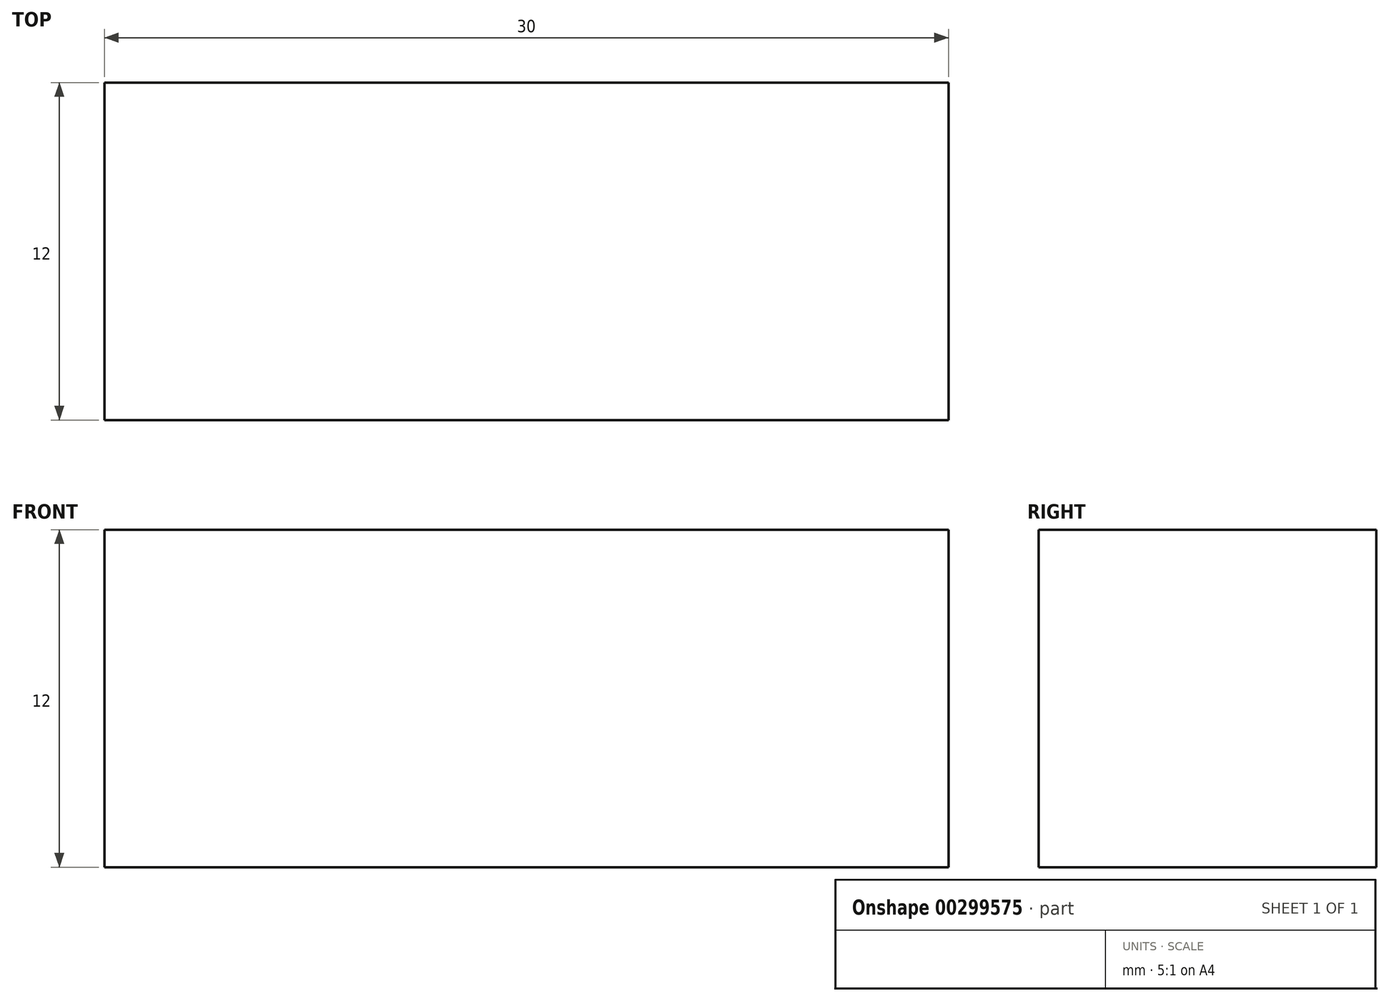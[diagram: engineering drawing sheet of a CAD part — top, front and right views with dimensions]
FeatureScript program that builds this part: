
annotation { "Feature Type Name" : "Feature", "Feature Type Description" : "" }
export const myFeature = defineFeature(function(context is Context, id is Id, definition is map)
    precondition{}
    {
        {
            var Q0;
            Q0=qCreatedBy(makeId("Front.planeOp"),FACE);
            var sketch = newSketch(context, id + "F0", { "sketchPlane" : qUnion([Q0])});
            skLineSegment(sketch, "E0.bottom", {"start": v(0, 0) * mm, "end": v(30, 0) * mm});
            skLineSegment(sketch, "E0.top", {"start": v(0, 12) * mm, "end": v(30, 12) * mm});
            skLineSegment(sketch, "E0.left", {"start": v(0, 0) * mm, "end": v(0, 12) * mm});
            skLineSegment(sketch, "E0.right", {"start": v(30, 0) * mm, "end": v(30, 12) * mm});
            skSolve(sketch);
        }
        {
            var Q0;
            Q0 = qSketchRegion(id + "F0", true);
            extrude(context, id + "F1", {"entities" : qUnion([Q0]), "depth" : 12 * mm});
        }
    });
